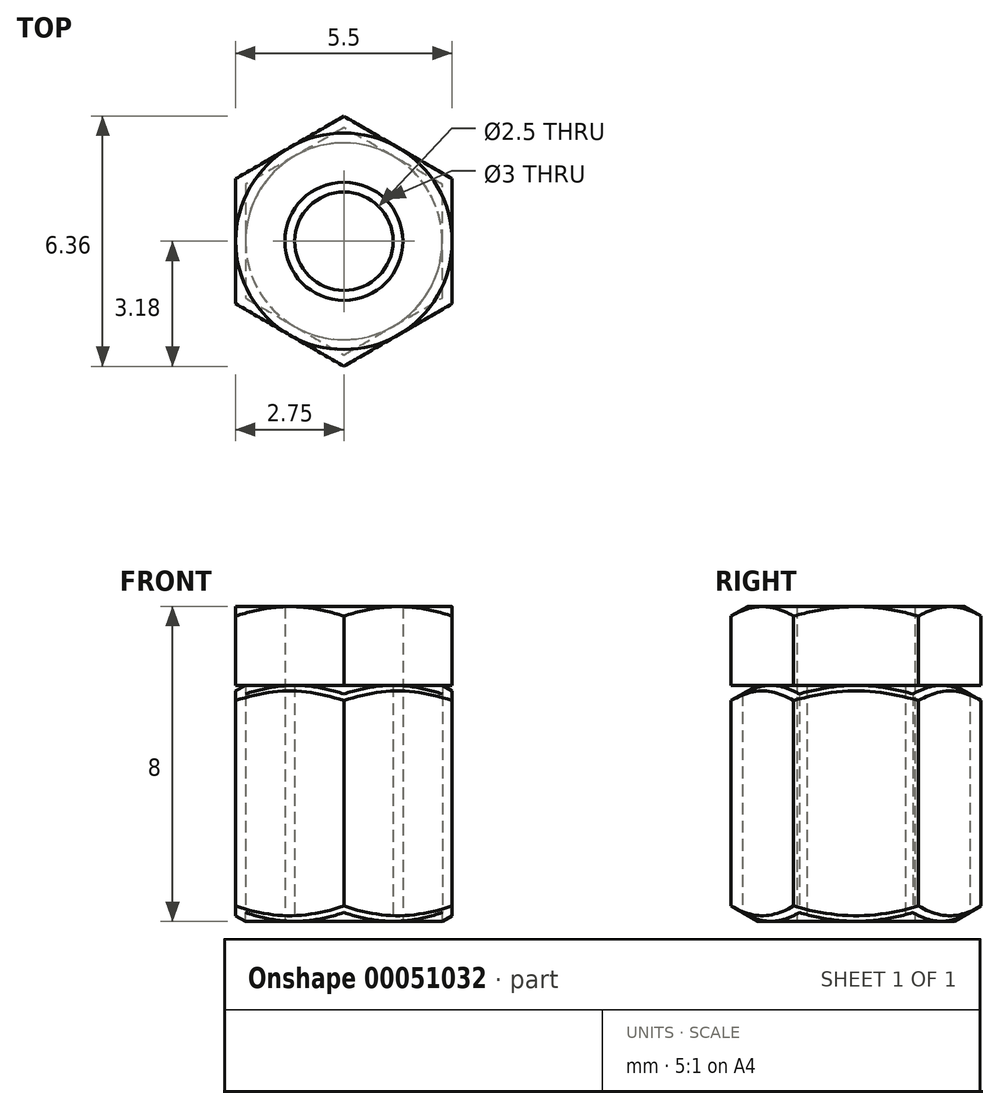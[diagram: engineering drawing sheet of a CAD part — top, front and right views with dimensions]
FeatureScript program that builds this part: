
annotation { "Feature Type Name" : "Feature", "Feature Type Description" : "" }
export const myFeature = defineFeature(function(context is Context, id is Id, definition is map)
    precondition{}
    {
        {
            assignVariable(context, id + "F0", {"name" : "LENGTH", "anyValue" : 8});
        }
        {
            var Q0;
            Q0=qCreatedBy(makeId("Top.planeOp"),FACE);
            var sketch = newSketch(context, id + "F1", { "sketchPlane" : qUnion([Q0])});
            skCircle(sketch, "E0.cCircle", {"center": v(0, 0) * mm, "radius": 2.75 * mm, "construction": true});
            skLineSegment(sketch, "E0.0", {"start": v(0, 3.18) * mm, "end": v(2.75, 1.59) * mm});
            skLineSegment(sketch, "E0.1", {"start": v(2.75, 1.59) * mm, "end": v(2.75, -1.59) * mm});
            skLineSegment(sketch, "E0.2", {"start": v(2.75, -1.59) * mm, "end": v(0, -3.18) * mm});
            skLineSegment(sketch, "E0.3", {"start": v(0, -3.18) * mm, "end": v(-2.75, -1.59) * mm});
            skLineSegment(sketch, "E0.4", {"start": v(-2.75, -1.59) * mm, "end": v(-2.75, 1.59) * mm});
            skLineSegment(sketch, "E0.5", {"start": v(-2.75, 1.59) * mm, "end": v(0, 3.18) * mm});
            skPoint(sketch, "E0.0.midPoint", {"position": v(1.38, 2.38) * mm});
            skCircle(sketch, "E1", {"center": v(0, 0) * mm, "radius": 1.5 * mm});
            skSolve(sketch);
        }
        {
            var Q0;
            Q0=makeQuery(id+"F1.imprint","IMPRINT",FACE,{"disambiguationData":[TD([[makeQuery(id+"F1.imprint","IMPRINT",EDGE,{"derivedFrom":sQuery(id+"F1.wireOp",EDGE,"E0.0")}),-1.0]])]});
            extrude(context, id + "F2", {"entities" : qUnion([Q0]), "depth" : (getVariable(context, 'LENGTH')) * mm});
        }
        {
            var Q0;
            Q0=qCreatedBy(makeId("Front.planeOp"),FACE);
            var sketch = newSketch(context, id + "F3", { "sketchPlane" : qUnion([Q0])});
            skLineSegment(sketch, "E2.0", {"start": v(0, 8) * mm, "end": v(0, 0) * mm, "construction": true});
            skLineSegment(sketch, "E3", {"start": v(0, 4) * mm, "end": v(2.75, 4) * mm, "construction": true});
            skLineSegment(sketch, "E4", {"start": v(2.75, 8) * mm, "end": v(5.48, 8) * mm});
            skLineSegment(sketch, "E5", {"start": v(5.48, 8) * mm, "end": v(5.48, 6.42) * mm});
            skLineSegment(sketch, "E6", {"start": v(5.48, 6.42) * mm, "end": v(2.75, 8) * mm});
            skLineSegment(sketch, "E7.MirrorCS", {"start": v(2.75, 0) * mm, "end": v(5.48, 0) * mm});
            skLineSegment(sketch, "E8.MirrorCS", {"start": v(5.48, 1.58) * mm, "end": v(2.75, 0) * mm});
            skLineSegment(sketch, "E9.MirrorCS", {"start": v(5.48, 0) * mm, "end": v(5.48, 1.58) * mm});
            skSolve(sketch);
        }
        {
            var Q0;
            Q0 = qSketchRegion(id + "F3", true);
            var Q1;
            Q1=sQuery(id+"F3.wireOp",EDGE,"E2.0");
            revolve(context, id + "F4", {"operationType" : NewBodyOperationType.REMOVE, "entities" : qUnion([Q0]), "axis" : qUnion([Q1]), "revolveType" : RevolveType.FULL, "oppositeDirection" : true});
        }
        {
            var Q0;
            Q0=qCreatedBy(makeId("Top.planeOp"),FACE);
            var sketch = newSketch(context, id + "F5", { "sketchPlane" : qUnion([Q0])});
            skCircle(sketch, "E10.cCircle", {"center": v(0, 0) * mm, "radius": 2.5 * mm, "construction": true});
            skLineSegment(sketch, "E10.0", {"start": v(2.5, -1.44) * mm, "end": v(0, -2.89) * mm});
            skLineSegment(sketch, "E10.1", {"start": v(0, -2.89) * mm, "end": v(-2.5, -1.44) * mm});
            skLineSegment(sketch, "E10.2", {"start": v(-2.5, -1.44) * mm, "end": v(-2.5, 1.44) * mm});
            skLineSegment(sketch, "E10.3", {"start": v(-2.5, 1.44) * mm, "end": v(0, 2.89) * mm});
            skLineSegment(sketch, "E10.4", {"start": v(0, 2.89) * mm, "end": v(2.5, 1.44) * mm});
            skLineSegment(sketch, "E10.5", {"start": v(2.5, 1.44) * mm, "end": v(2.5, -1.44) * mm});
            skPoint(sketch, "E10.0.midPoint", {"position": v(1.25, -2.17) * mm});
            skCircle(sketch, "E11", {"center": v(0, 0) * mm, "radius": 1.25 * mm});
            skSolve(sketch);
        }
        {
            var Q0;
            Q0=makeQuery(id+"F5.imprint","IMPRINT",FACE,{"disambiguationData":[TD([[makeQuery(id+"F5.imprint","IMPRINT",EDGE,{"derivedFrom":sQuery(id+"F5.wireOp",EDGE,"E10.0")}),-1.0]])]});
            extrude(context, id + "F6", {"entities" : qUnion([Q0]), "depth" : 6 * mm});
        }
        {
            var Q0;
            Q0=qCreatedBy(makeId("Front.planeOp"),FACE);
            var sketch = newSketch(context, id + "F7", { "sketchPlane" : qUnion([Q0])});
            skLineSegment(sketch, "E12.0", {"start": v(0, 6) * mm, "end": v(0, 0) * mm, "construction": true});
            skLineSegment(sketch, "E13", {"start": v(0, 3) * mm, "end": v(2.5, 3) * mm, "construction": true});
            skLineSegment(sketch, "E14", {"start": v(2.5, 6) * mm, "end": v(4.4, 4.9) * mm});
            skLineSegment(sketch, "E15", {"start": v(4.4, 4.9) * mm, "end": v(4.4, 6) * mm});
            skLineSegment(sketch, "E16", {"start": v(4.4, 6) * mm, "end": v(2.5, 6) * mm});
            skLineSegment(sketch, "E17.MirrorCS", {"start": v(4.4, 0) * mm, "end": v(2.5, 0) * mm});
            skLineSegment(sketch, "E18.MirrorCS", {"start": v(4.4, 1.1) * mm, "end": v(4.4, 0) * mm});
            skLineSegment(sketch, "E19.MirrorCS", {"start": v(2.5, 0) * mm, "end": v(4.4, 1.1) * mm});
            skSolve(sketch);
        }
        {
            var Q0;
            Q0 = qSketchRegion(id + "F7", true);
            var Q1;
            Q1=sQuery(id+"F7.wireOp",EDGE,"E12.0");
            revolve(context, id + "F8", {"operationType" : NewBodyOperationType.REMOVE, "entities" : qUnion([Q0]), "axis" : qUnion([Q1]), "revolveType" : RevolveType.FULL, "oppositeDirection" : true});
        }
    });
